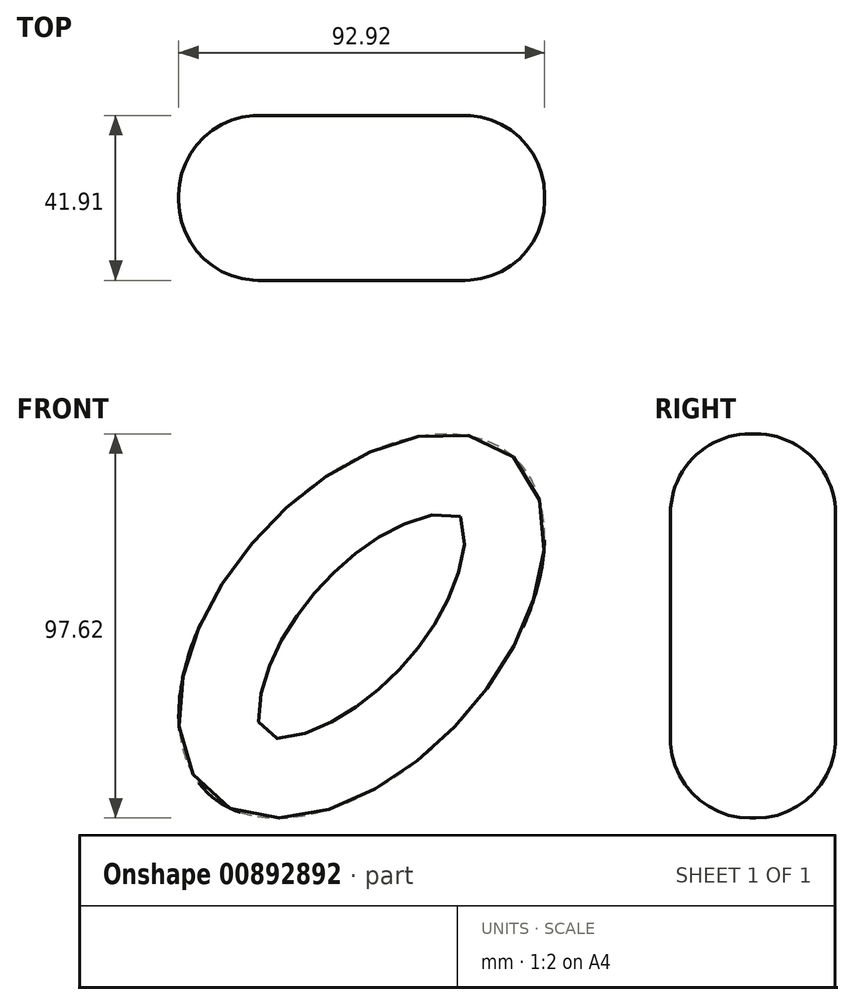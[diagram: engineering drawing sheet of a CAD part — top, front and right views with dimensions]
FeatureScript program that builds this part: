
annotation { "Feature Type Name" : "Feature", "Feature Type Description" : "" }
export const myFeature = defineFeature(function(context is Context, id is Id, definition is map)
    precondition{}
    {
        {
            var Q0;
            Q0=qCreatedBy(makeId("Front.planeOp"),FACE);
            var sketch = newSketch(context, id + "F0", { "sketchPlane" : qUnion([Q0])});
            skEllipse(sketch, "E0", {"center": v(0, 0) * mm, "majorRadius": 34.77 * mm, "minorRadius": 57.72 * mm, "majorAxis": v(0.74, -0.67)});
            skSolve(sketch);
        }
        {
            var Q0;
            Q0 = qSketchRegion(id + "F0", true);
            extrude(context, id + "F1", {"entities" : qUnion([Q0]), "depth" : 41.9 * mm, "offsetDistance" : 25.4 * mm});
        }
        {
            var Q0;
            Q0=makeQuery(id+"F1.opExtrude","CAP_FACE",FACE,{"disambiguationData":[OSD([sQuery(id+"F0.wireOp",EDGE,"E0")])],"isStart":false});
            var Q1;
            Q1=makeQuery(id+"F1.opExtrude","CAP_EDGE",EDGE,{"disambiguationData":[OSD([sQuery(id+"F0.wireOp",EDGE,"E0")])],"isStart":true});
            fillet(context, id + "F2", {"entities" : qUnion([Q0, Q1]), "radius" : 20.24 * mm, "tangentPropagation" : true, "allowEdgeOverflow" : false});
        }
    });
